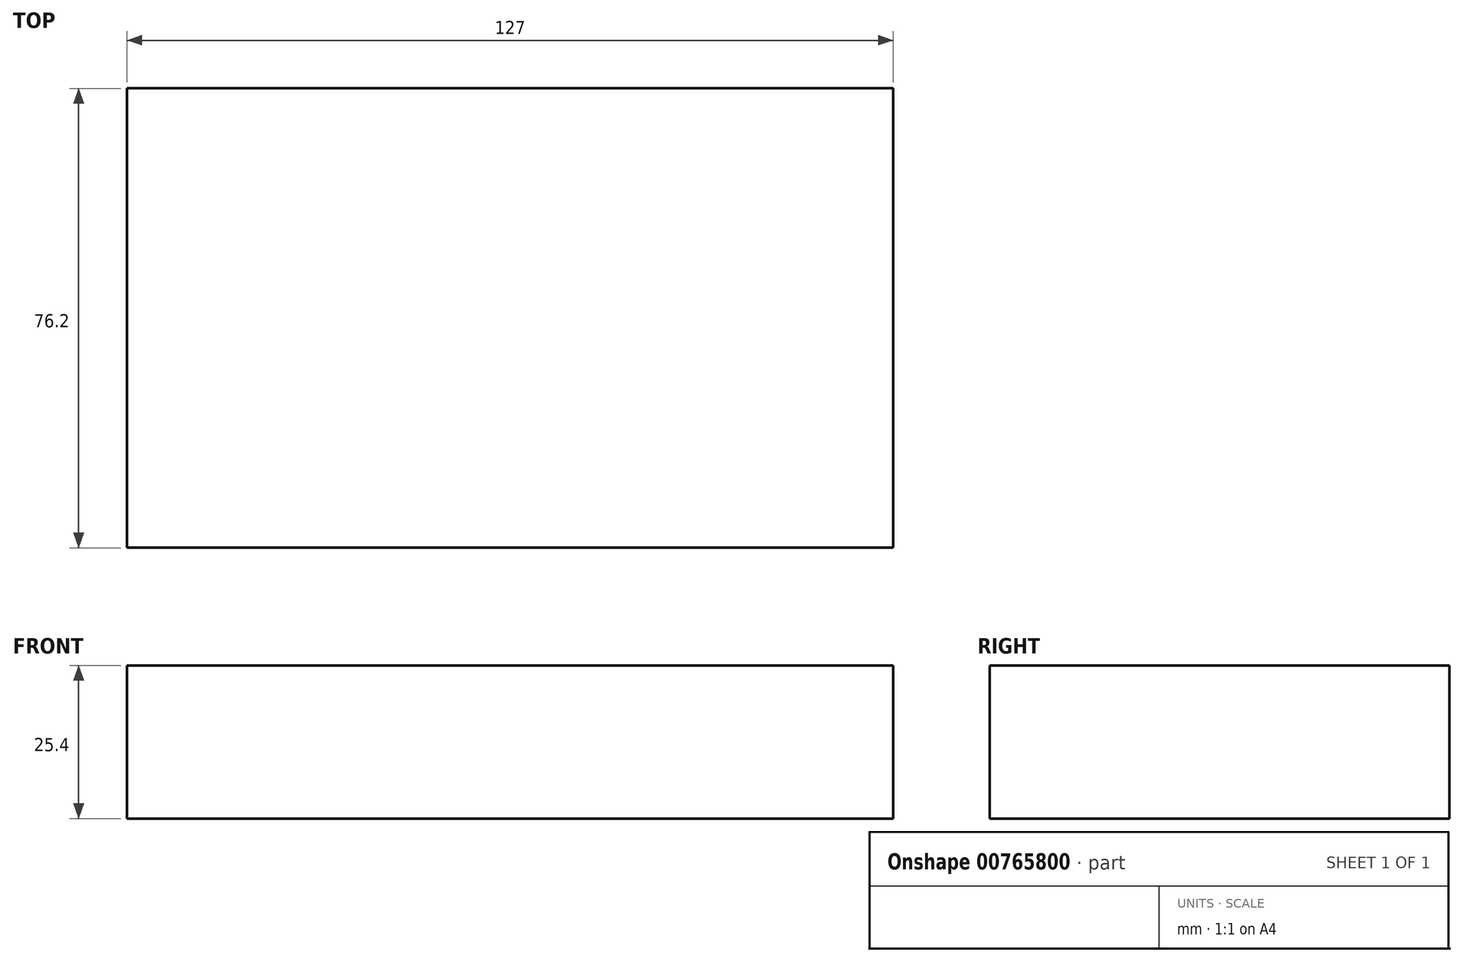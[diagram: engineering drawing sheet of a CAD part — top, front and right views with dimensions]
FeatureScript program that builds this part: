
annotation { "Feature Type Name" : "Feature", "Feature Type Description" : "" }
export const myFeature = defineFeature(function(context is Context, id is Id, definition is map)
    precondition{}
    {
        {
            var Q0;
            Q0=qCreatedBy(makeId("Top.planeOp"),FACE);
            var sketch = newSketch(context, id + "F0", { "sketchPlane" : qUnion([Q0])});
            skLineSegment(sketch, "E0.bottom", {"start": v(-106.08, 20.54) * mm, "end": v(20.92, 20.54) * mm});
            skLineSegment(sketch, "E0.top", {"start": v(-106.08, -55.66) * mm, "end": v(20.92, -55.66) * mm});
            skLineSegment(sketch, "E0.left", {"start": v(-106.08, 20.54) * mm, "end": v(-106.08, -55.66) * mm});
            skLineSegment(sketch, "E0.right", {"start": v(20.92, 20.54) * mm, "end": v(20.92, -55.66) * mm});
            skSolve(sketch);
        }
        {
            var Q0;
            Q0 = qSketchRegion(id + "F0", true);
            extrude(context, id + "F1", {"entities" : qUnion([Q0]), "depth" : 25.4 * mm, "offsetDistance" : 25.4 * mm});
        }
    });
